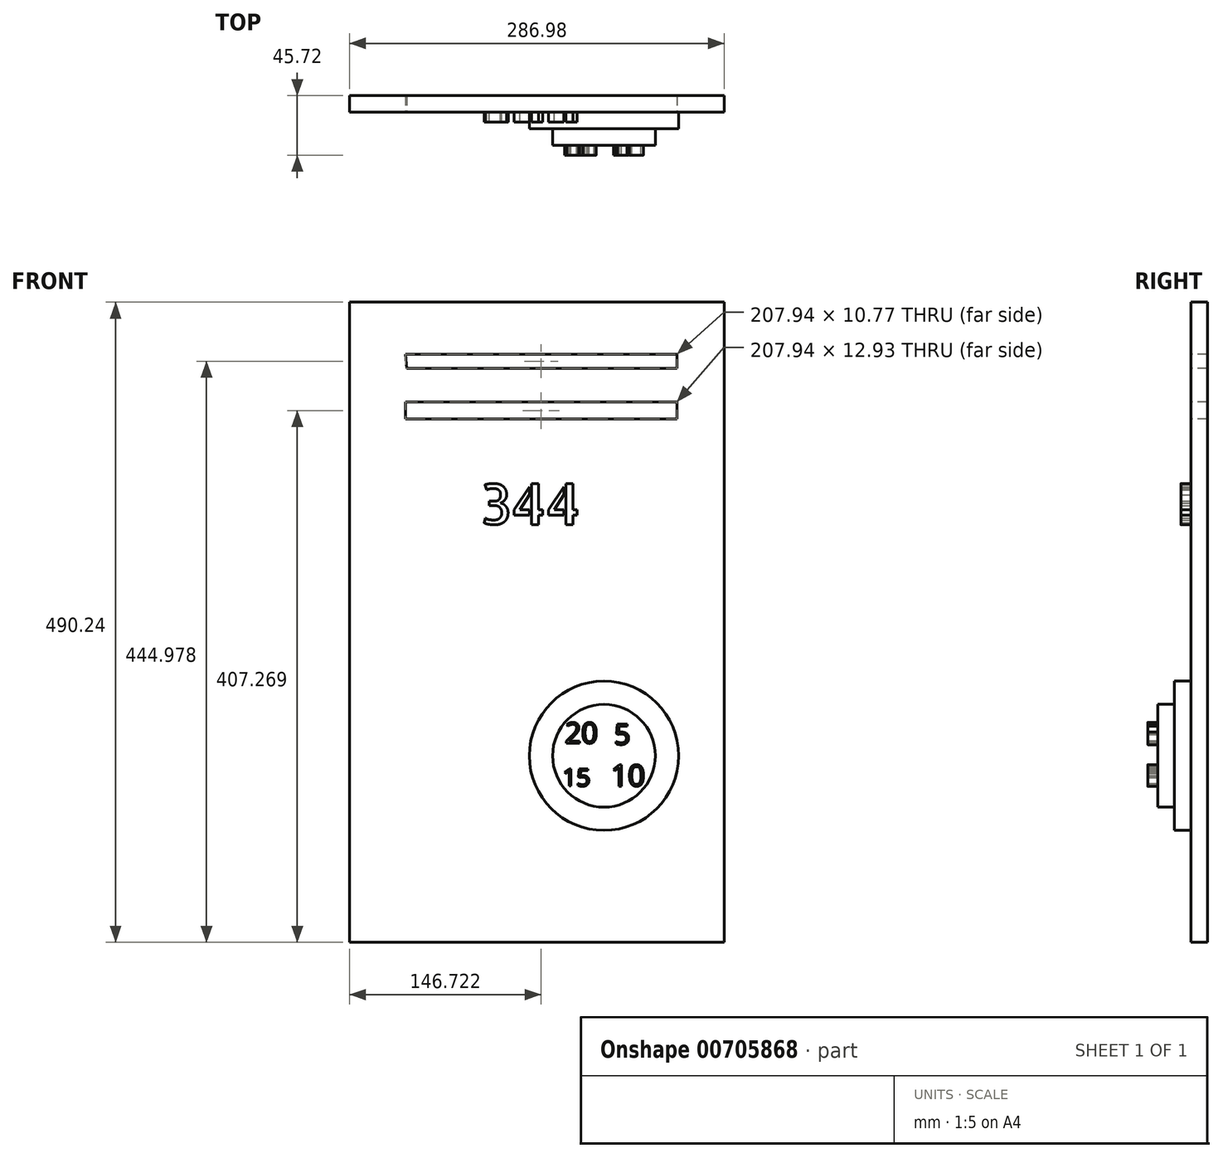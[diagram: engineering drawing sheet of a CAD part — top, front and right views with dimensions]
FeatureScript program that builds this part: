
annotation { "Feature Type Name" : "Feature", "Feature Type Description" : "" }
export const myFeature = defineFeature(function(context is Context, id is Id, definition is map)
    precondition{}
    {
        {
            var Q0;
            Q0=qCreatedBy(makeId("Front.planeOp"),FACE);
            var sketch = newSketch(context, id + "F0", { "sketchPlane" : qUnion([Q0])});
            skLineSegment(sketch, "E0.bottom", {"start": v(143.5, 245.12) * mm, "end": v(-143.5, 245.12) * mm});
            skLineSegment(sketch, "E0.top", {"start": v(143.5, -245.12) * mm, "end": v(-143.5, -245.12) * mm});
            skLineSegment(sketch, "E0.left", {"start": v(143.5, 245.12) * mm, "end": v(143.5, -245.12) * mm});
            skLineSegment(sketch, "E0.right", {"start": v(-143.5, 245.12) * mm, "end": v(-143.5, -245.12) * mm});
            skPoint(sketch, "E0.middle", {"position": v(0, 0) * mm});
            skLineSegment(sketch, "E1", {"start": v(-100.9, 145.77) * mm, "end": v(93.24, 145.77) * mm});
            skLineSegment(sketch, "E2", {"start": v(-102.04, 86.38) * mm, "end": v(93.24, 86.38) * mm});
            skSolve(sketch);
        }
        {
            var Q0;
            Q0 = qSketchRegion(id + "F0", true);
            extrude(context, id + "F1", {"entities" : qUnion([Q0]), "oppositeDirection" : true, "depth" : 12.7 * mm, "offsetDistance" : 25.4 * mm});
        }
        {
            var Q0;
            Q0=makeQuery(id+"F1.opExtrude","CAP_FACE",FACE,{"disambiguationData":[OSD([sQuery(id+"F0.wireOp",EDGE,"E0.bottom"),sQuery(id+"F0.wireOp",EDGE,"E0.top"),sQuery(id+"F0.wireOp",EDGE,"E0.left"),sQuery(id+"F0.wireOp",EDGE,"E0.right")])],"isStart":true});
            var sketch = newSketch(context, id + "F2", { "sketchPlane" : qUnion([Q0])});
            skText(sketch, "E3", { "text": "344", "fontName": "AllertaStencil-Regular.ttf"});
            const initialGuessF2  = {"E3": [-0.04363, 0.07488, 1, 0, 0.03124]};
            skSetInitialGuess(sketch, initialGuessF2);
            skSolve(sketch);
        }
        {
            var Q0;
            Q0 = qSketchRegion(id + "F2", true);
            extrude(context, id + "F3", {"entities" : qUnion([Q0]), "operationType" : NewBodyOperationType.ADD, "depth" : 7.62 * mm, "offsetDistance" : 25.4 * mm});
        }
        {
            var Q0;
            Q0=makeQuery(id+"F1.opExtrude","CAP_FACE",FACE,{"disambiguationData":[OSD([sQuery(id+"F0.wireOp",EDGE,"E0.bottom"),sQuery(id+"F0.wireOp",EDGE,"E0.top"),sQuery(id+"F0.wireOp",EDGE,"E0.left"),sQuery(id+"F0.wireOp",EDGE,"E0.right")])],"isStart":true});
            var sketch = newSketch(context, id + "F4", { "sketchPlane" : qUnion([Q0])});
            skLineSegment(sketch, "E4", {"start": v(-100.74, 205.25) * mm, "end": v(107.2, 205.25) * mm});
            skLineSegment(sketch, "E5", {"start": v(107.2, 205.25) * mm, "end": v(107.2, 194.47) * mm});
            skLineSegment(sketch, "E6", {"start": v(107.2, 194.47) * mm, "end": v(-99.66, 194.47) * mm});
            skLineSegment(sketch, "E7", {"start": v(-99.66, 194.47) * mm, "end": v(-100.74, 205.25) * mm});
            skLineSegment(sketch, "E8", {"start": v(107.2, 168.61) * mm, "end": v(-100.74, 168.61) * mm});
            skLineSegment(sketch, "E9", {"start": v(107.2, 168.61) * mm, "end": v(107.2, 155.68) * mm});
            skLineSegment(sketch, "E10", {"start": v(107.2, 155.68) * mm, "end": v(-100.74, 155.68) * mm});
            skLineSegment(sketch, "E11", {"start": v(-100.74, 155.68) * mm, "end": v(-100.74, 168.61) * mm});
            skSolve(sketch);
        }
        {
            var Q0;
            Q0=makeQuery(id+"F4.imprint","IMPRINT",FACE,{"disambiguationData":[TD([[makeQuery(id+"F4.imprint","IMPRINT",EDGE,{"derivedFrom":sQuery(id+"F4.wireOp",EDGE,"E8")}),1.0]])]});
            var Q1;
            Q1=makeQuery(id+"F4.imprint","IMPRINT",FACE,{"disambiguationData":[TD([[makeQuery(id+"F4.imprint","IMPRINT",EDGE,{"derivedFrom":sQuery(id+"F4.wireOp",EDGE,"E4")}),-1.0]])]});
            extrude(context, id + "F5", {"entities" : qUnion([Q0, Q1]), "operationType" : NewBodyOperationType.REMOVE, "oppositeDirection" : true, "depth" : 25.4 * mm, "offsetDistance" : 25.4 * mm});
        }
        {
            var Q0;
            Q0=makeQuery(id+"F1.opExtrude","CAP_FACE",FACE,{"disambiguationData":[OSD([sQuery(id+"F0.wireOp",EDGE,"E0.bottom"),sQuery(id+"F0.wireOp",EDGE,"E0.top"),sQuery(id+"F0.wireOp",EDGE,"E0.left"),sQuery(id+"F0.wireOp",EDGE,"E0.right")])],"isStart":true});
            var sketch = newSketch(context, id + "F6", { "sketchPlane" : qUnion([Q0])});
            skCircle(sketch, "E12", {"center": v(51.37, -102.21) * mm, "radius": 57.16 * mm});
            skSolve(sketch);
        }
        {
            var Q0;
            Q0 = qSketchRegion(id + "F6", true);
            extrude(context, id + "F7", {"entities" : qUnion([Q0]), "operationType" : NewBodyOperationType.ADD, "depth" : 12.7 * mm, "offsetDistance" : 25.4 * mm});
        }
        {
            var Q0;
            Q0=makeQuery(id+"F7.opExtrude","CAP_FACE",FACE,{"disambiguationData":[OSD([sQuery(id+"F6.wireOp",EDGE,"E12")])],"isStart":false});
            var sketch = newSketch(context, id + "F8", { "sketchPlane" : qUnion([Q0])});
            skCircle(sketch, "E13", {"center": v(51.37, -102.21) * mm, "radius": 39.34 * mm});
            skSolve(sketch);
        }
        {
            var Q0;
            Q0 = qSketchRegion(id + "F8", true);
            extrude(context, id + "F9", {"entities" : qUnion([Q0]), "operationType" : NewBodyOperationType.ADD, "depth" : 12.7 * mm, "offsetDistance" : 25.4 * mm});
        }
        {
            var Q0;
            Q0=makeQuery(id+"F9.opExtrude","CAP_FACE",FACE,{"disambiguationData":[OSD([sQuery(id+"F8.wireOp",EDGE,"E13")])],"isStart":false});
            var sketch = newSketch(context, id + "F10", { "sketchPlane" : qUnion([Q0])});
            skText(sketch, "E14", { "text": "5", "fontName": "OpenSans-Regular.ttf"});
            const initialGuessF10  = {"E14": [0.05917, -0.09355, 1, 0, 0.01557]};
            skSetInitialGuess(sketch, initialGuessF10);
            skSolve(sketch);
        }
        {
            var Q0;
            Q0 = qSketchRegion(id + "F10", true);
            extrude(context, id + "F11", {"entities" : qUnion([Q0]), "operationType" : NewBodyOperationType.ADD, "depth" : 7.62 * mm, "offsetDistance" : 25.4 * mm});
        }
        {
            var Q0;
            Q0=makeQuery(id+"F9.opExtrude","CAP_FACE",FACE,{"disambiguationData":[OSD([sQuery(id+"F8.wireOp",EDGE,"E13")])],"isStart":false});
            var sketch = newSketch(context, id + "F12", { "sketchPlane" : qUnion([Q0])});
            skText(sketch, "E15", { "text": "10", "fontName": "OpenSans-Regular.ttf"});
            const initialGuessF12  = {"E15": [0.05672, -0.12547, 1, 0, 0.0164]};
            skSetInitialGuess(sketch, initialGuessF12);
            skSolve(sketch);
        }
        {
            var Q0;
            Q0 = qSketchRegion(id + "F12", true);
            extrude(context, id + "F13", {"entities" : qUnion([Q0]), "operationType" : NewBodyOperationType.ADD, "depth" : 7.62 * mm, "offsetDistance" : 25.4 * mm});
        }
        {
            var Q0;
            {var subQ0=sQuery(id+"F8.wireOp",EDGE,"E13");Q0=makeQuery(id+"F13.boolean.opBoolean","SPLIT",FACE,{"disambiguationData":[TD([makeQuery(id+"F9.opExtrude","SWEPT_FACE",FACE,{"disambiguationData":[OSD([subQ0])]})])],"derivedFrom":makeQuery(id+"F9.opExtrude","CAP_FACE",FACE,{"disambiguationData":[OSD([subQ0])],"isStart":false})});}
            var sketch = newSketch(context, id + "F14", { "sketchPlane" : qUnion([Q0])});
            skText(sketch, "E16", { "text": "15", "fontName": "OpenSans-Regular.ttf"});
            const initialGuessF14  = {"E16": [0.01963, -0.12545, 1, 0, 0.0134]};
            skSetInitialGuess(sketch, initialGuessF14);
            skSolve(sketch);
        }
        {
            var Q0;
            Q0 = qSketchRegion(id + "F14", true);
            extrude(context, id + "F15", {"entities" : qUnion([Q0]), "operationType" : NewBodyOperationType.ADD, "depth" : 7.62 * mm, "offsetDistance" : 25.4 * mm});
        }
        {
            var Q0;
            {var subQ0=sQuery(id+"F8.wireOp",EDGE,"E13");Q0=makeQuery(id+"F13.boolean.opBoolean","SPLIT",FACE,{"disambiguationData":[TD([makeQuery(id+"F9.opExtrude","SWEPT_FACE",FACE,{"disambiguationData":[OSD([subQ0])]})])],"derivedFrom":makeQuery(id+"F9.opExtrude","CAP_FACE",FACE,{"disambiguationData":[OSD([subQ0])],"isStart":false})});}
            var sketch = newSketch(context, id + "F16", { "sketchPlane" : qUnion([Q0])});
            skText(sketch, "E17", { "text": "20", "fontName": "OpenSans-Regular.ttf"});
            const initialGuessF16  = {"E17": [0.02142, -0.09257, 1, 0, 0.01586]};
            skSetInitialGuess(sketch, initialGuessF16);
            skSolve(sketch);
        }
        {
            var Q0;
            Q0 = qSketchRegion(id + "F16", true);
            extrude(context, id + "F17", {"entities" : qUnion([Q0]), "operationType" : NewBodyOperationType.ADD, "depth" : 7.62 * mm, "offsetDistance" : 25.4 * mm});
        }
    });
